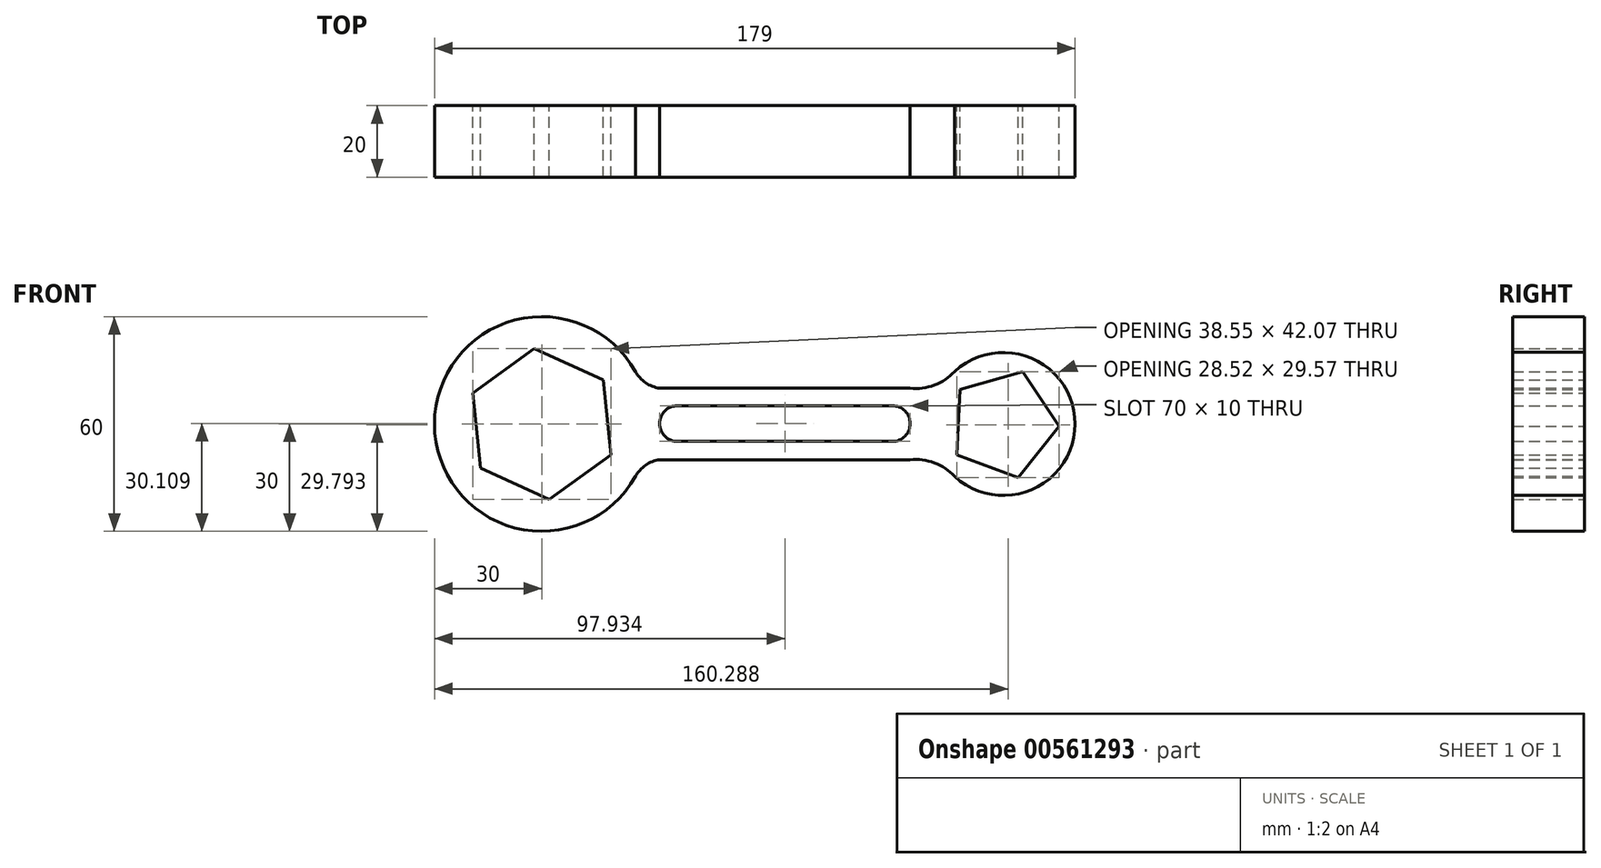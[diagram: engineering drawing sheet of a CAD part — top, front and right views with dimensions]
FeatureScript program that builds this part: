
annotation { "Feature Type Name" : "Feature", "Feature Type Description" : "" }
export const myFeature = defineFeature(function(context is Context, id is Id, definition is map)
    precondition{}
    {
        {
            var Q0;
            Q0=qCreatedBy(makeId("Front.planeOp"),FACE);
            var sketch = newSketch(context, id + "F0", { "sketchPlane" : qUnion([Q0])});
            skCircle(sketch, "E0", {"center": v(-44.94, 0) * mm, "radius": 30 * mm});
            skCircle(sketch, "E1", {"center": v(84.06, 0) * mm, "radius": 20 * mm});
            skLineSegment(sketch, "E2", {"start": v(-51.33, 17.16) * mm, "end": v(-51.57, 17.79) * mm});
            skLineSegment(sketch, "E3", {"start": v(84.06, 0) * mm, "end": v(95.43, 16.45) * mm});
            skCircle(sketch, "E4.cCircle", {"center": v(-44.94, 0) * mm, "radius": 18.31 * mm, "construction": true});
            skLineSegment(sketch, "E4.0", {"start": v(-47.05, 21.04) * mm, "end": v(-27.78, 12.35) * mm});
            skLineSegment(sketch, "E4.1", {"start": v(-27.78, 12.35) * mm, "end": v(-25.66, -8.69) * mm});
            skLineSegment(sketch, "E4.2", {"start": v(-25.66, -8.69) * mm, "end": v(-42.83, -21.04) * mm});
            skLineSegment(sketch, "E4.3", {"start": v(-42.83, -21.04) * mm, "end": v(-62.1, -12.35) * mm});
            skLineSegment(sketch, "E4.4", {"start": v(-62.1, -12.35) * mm, "end": v(-64.21, 8.69) * mm});
            skLineSegment(sketch, "E4.5", {"start": v(-64.21, 8.69) * mm, "end": v(-47.05, 21.04) * mm});
            skPoint(sketch, "E4.0.midPoint", {"position": v(-37.41, 16.7) * mm});
            skCircle(sketch, "E5.cCircle", {"center": v(84.06, 0) * mm, "radius": 12.6 * mm, "construction": true});
            skLineSegment(sketch, "E5.0", {"start": v(71.88, 9.68) * mm, "end": v(89.5, 14.58) * mm});
            skLineSegment(sketch, "E5.1", {"start": v(89.5, 14.58) * mm, "end": v(99.6, -0.67) * mm});
            skLineSegment(sketch, "E5.2", {"start": v(99.6, -0.67) * mm, "end": v(88.23, -15) * mm});
            skLineSegment(sketch, "E5.3", {"start": v(88.23, -15) * mm, "end": v(71.09, -8.6) * mm});
            skLineSegment(sketch, "E5.4", {"start": v(71.09, -8.6) * mm, "end": v(71.88, 9.68) * mm});
            skPoint(sketch, "E5.0.midPoint", {"position": v(80.69, 12.13) * mm});
            skLineSegment(sketch, "E6", {"start": v(-31.34, 12.26) * mm, "end": v(-30.08, 13.39) * mm});
            skLineSegment(sketch, "E7", {"start": v(-26.63, 0) * mm, "end": v(-26.54, 0) * mm});
            skLineSegment(sketch, "E8", {"start": v(-12, 10) * mm, "end": v(61.04, 10) * mm});
            skLineSegment(sketch, "E9", {"start": v(61.04, -10) * mm, "end": v(-12, -10) * mm});
            skLineSegment(sketch, "E10", {"start": v(-7, 5.1) * mm, "end": v(53, 5.1) * mm});
            skLineSegment(sketch, "E11", {"start": v(53, -4.9) * mm, "end": v(-7, -4.9) * mm});
            skArc(sketch, "E12", {"start": v(-7, 5.1) * mm, "mid": v(-12, 0.1) * mm, "end": v(-7, -4.9) * mm});
            skArc(sketch, "E13", {"start": v(53, -4.9) * mm, "mid": v(58, 0.1) * mm, "end": v(53, 5.1) * mm});
            skArc(sketch, "E14", {"start": v(-18.76, 14.65) * mm, "mid": v(-15.94, 11.51) * mm, "end": v(-12, 10) * mm});
            skArc(sketch, "E15", {"start": v(-12, -10) * mm, "mid": v(-15.94, -11.51) * mm, "end": v(-18.76, -14.65) * mm});
            skArc(sketch, "E16", {"start": v(58, 10) * mm, "mid": v(64.76, 10.87) * mm, "end": v(70.45, 14.65) * mm});
            skArc(sketch, "E17", {"start": v(70.45, -14.65) * mm, "mid": v(64.76, -10.87) * mm, "end": v(58, -10) * mm});
            skLineSegment(sketch, "E18.trimOffspring", {"start": v(71.46, 0) * mm, "end": v(71.47, 0) * mm});
            skPoint(sketch, "E19.end.orphan", {"position": v(-12, 0.1) * mm});
            skPoint(sketch, "E20.trimOffspring.end.orphan", {"position": v(58, 0.1) * mm});
            skPoint(sketch, "E21.orphan", {"position": v(66.74, 10) * mm});
            skPoint(sketch, "E22.orphan", {"position": v(66.74, -10) * mm});
            skPoint(sketch, "E23.end.orphan", {"position": v(71.83, 8.69) * mm});
            skSolve(sketch);
        }
        {
            var Q0;
            {var subQ3=sQuery(id+"F0.wireOp",EDGE,"E4.2");Q0=makeQuery(id+"F0.imprint","IMPRINT",FACE,{"disambiguationData":[TD([[makeQuery(id+"F0.imprint","IMPRINT",EDGE,{"derivedFrom":subQ3}),1.0]])]});}
            var Q1;
            {var subQ1=sQuery(id+"F0.wireOp",EDGE,"E5.0");Q1=makeQuery(id+"F0.imprint","IMPRINT",FACE,{"disambiguationData":[TD([[makeQuery(id+"F0.imprint","IMPRINT",EDGE,{"derivedFrom":subQ1}),1.0]])]});}
            var Q2;
            Q2=makeQuery(id+"F0.imprint","IMPRINT",FACE,{"disambiguationData":[TD([[makeQuery(id+"F0.imprint","IMPRINT",EDGE,{"derivedFrom":sQuery(id+"F0.wireOp",EDGE,"E10")}),1.0]])]});
            extrude(context, id + "F1", {"entities" : qUnion([Q0, Q1, Q2]), "depth" : 20 * mm, "offsetDistance" : 25 * mm});
        }
    });
